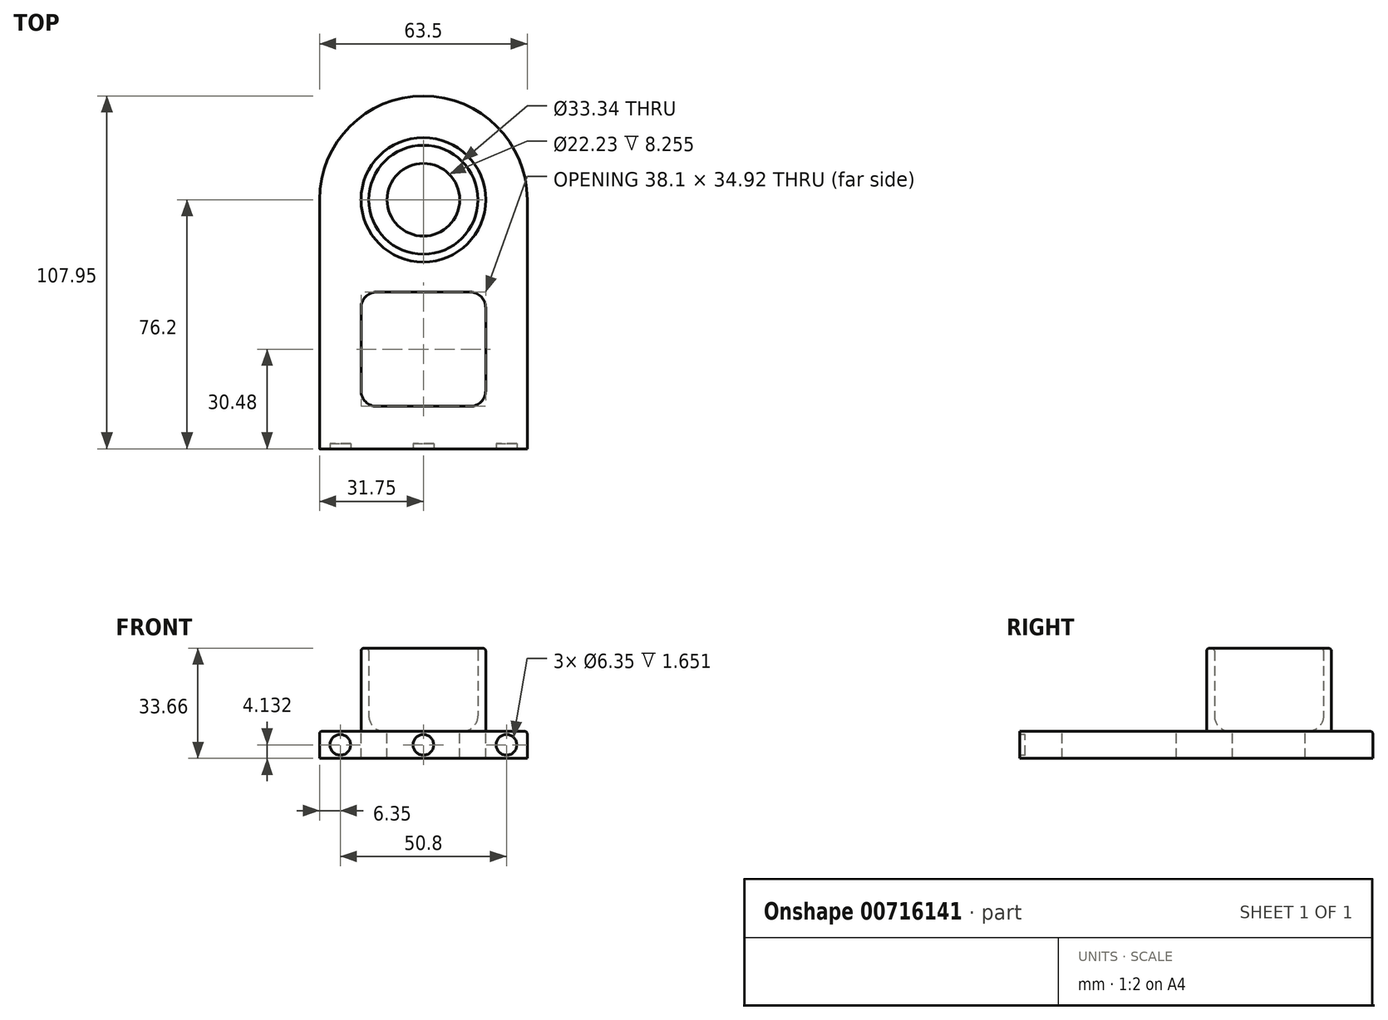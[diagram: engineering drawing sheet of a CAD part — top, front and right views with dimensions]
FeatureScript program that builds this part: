
annotation { "Feature Type Name" : "Feature", "Feature Type Description" : "" }
export const myFeature = defineFeature(function(context is Context, id is Id, definition is map)
    precondition{}
    {
        {
            var Q0;
            Q0=qCreatedBy(makeId("Top.planeOp"),FACE);
            var sketch = newSketch(context, id + "F0", { "sketchPlane" : qUnion([Q0])});
            skCircle(sketch, "E0", {"center": v(0, 0) * mm, "radius": 19.05 * mm, "construction": true});
            skArc(sketch, "E1", {"start": v(0, 31.75) * mm, "mid": v(-22.45, 22.45) * mm, "end": v(-31.75, 0) * mm});
            skLineSegment(sketch, "E2", {"start": v(-31.75, 0) * mm, "end": v(-31.75, -76.2) * mm});
            skLineSegment(sketch, "E3", {"start": v(-31.75, -76.2) * mm, "end": v(0, -76.2) * mm});
            skLineSegment(sketch, "E4", {"start": v(0, -76.2) * mm, "end": v(0, 0) * mm, "construction": true});
            skArc(sketch, "E5.MirrorCS", {"start": v(0, 31.75) * mm, "mid": v(22.45, 22.45) * mm, "end": v(31.75, 0) * mm});
            skLineSegment(sketch, "E6.MirrorCS", {"start": v(31.75, 0) * mm, "end": v(31.75, -76.2) * mm});
            skLineSegment(sketch, "E7.MirrorCS", {"start": v(31.75, -76.2) * mm, "end": v(0, -76.2) * mm});
            skSolve(sketch);
        }
        {
            var Q0;
            Q0 = qSketchRegion(id + "F0", true);
            extrude(context, id + "F1", {"entities" : qUnion([Q0]), "oppositeDirection" : true, "depth" : 8.25 * mm, "offsetDistance" : 25.4 * mm});
        }
        {
            var Q0;
            Q0=makeQuery(id+"F1.opExtrude","CAP_FACE",FACE,{"disambiguationData":[OSD([sQuery(id+"F0.wireOp",EDGE,"E1"),sQuery(id+"F0.wireOp",EDGE,"E2"),sQuery(id+"F0.wireOp",EDGE,"E3"),sQuery(id+"F0.wireOp",EDGE,"E5.MirrorCS"),sQuery(id+"F0.wireOp",EDGE,"E6.MirrorCS"),sQuery(id+"F0.wireOp",EDGE,"E7.MirrorCS")])],"isStart":true});
            var sketch = newSketch(context, id + "F2", { "sketchPlane" : qUnion([Q0])});
            skCircle(sketch, "E8", {"center": v(0, 0) * mm, "radius": 19.05 * mm});
            skCircle(sketch, "E9", {"center": v(0, 0) * mm, "radius": 16.67 * mm});
            skSolve(sketch);
        }
        {
            var Q0;
            Q0 = qSketchRegion(id + "F2", true);
            extrude(context, id + "F3", {"entities" : qUnion([Q0]), "operationType" : NewBodyOperationType.ADD, "depth" : 25.4 * mm, "offsetDistance" : 25.4 * mm});
        }
        {
            var Q0;
            Q0=makeQuery(id+"F1.opExtrude","SWEPT_FACE",FACE,{"disambiguationData":[OSD([sQuery(id+"F0.wireOp",EDGE,"E3"),sQuery(id+"F0.wireOp",EDGE,"E7.MirrorCS")])]});
            var sketch = newSketch(context, id + "F4", { "sketchPlane" : qUnion([Q0])});
            skCircle(sketch, "E10", {"center": v(-25.4, -4.13) * mm, "radius": 3.18 * mm});
            skCircle(sketch, "E11", {"center": v(0, -4.13) * mm, "radius": 3.18 * mm});
            skLineSegment(sketch, "E12", {"start": v(0, 0) * mm, "end": v(0, -8.26) * mm, "construction": true});
            skCircle(sketch, "E13.MirrorC", {"center": v(25.4, -4.13) * mm, "radius": 3.18 * mm});
            skSolve(sketch);
        }
        {
            var Q0;
            Q0 = qSketchRegion(id + "F4", true);
            extrude(context, id + "F5", {"entities" : qUnion([Q0]), "operationType" : NewBodyOperationType.REMOVE, "oppositeDirection" : true, "depth" : 1.65 * mm, "offsetDistance" : 25.4 * mm});
        }
        {
            var Q0;
            Q0=makeQuery(id+"F0.imprint","IMPRINT",FACE,{"disambiguationData":[TD([[makeQuery(id+"F0.imprint","IMPRINT",EDGE,{"derivedFrom":sQuery(id+"F0.wireOp",EDGE,"E1")}),1.0]])]});
            var sketch = newSketch(context, id + "F6", { "sketchPlane" : qUnion([Q0])});
            skLineSegment(sketch, "E14.bottom", {"start": v(-19.05, -63.18) * mm, "end": v(19.05, -63.18) * mm});
            skLineSegment(sketch, "E14.top", {"start": v(-19.05, -28.26) * mm, "end": v(19.05, -28.26) * mm});
            skLineSegment(sketch, "E14.left", {"start": v(-19.05, -63.18) * mm, "end": v(-19.05, -28.26) * mm});
            skLineSegment(sketch, "E14.right", {"start": v(19.05, -63.18) * mm, "end": v(19.05, -28.26) * mm});
            skPoint(sketch, "E14.middle", {"position": v(0, -45.72) * mm});
            skCircle(sketch, "E15", {"center": v(0, 0) * mm, "radius": 11.11 * mm});
            skSolve(sketch);
        }
        {
            var Q0;
            Q0 = qSketchRegion(id + "F6", true);
            extrude(context, id + "F7", {"entities" : qUnion([Q0]), "operationType" : NewBodyOperationType.REMOVE, "endBound" : BoundingType.UP_TO_NEXT, "oppositeDirection" : true, "depth" : 25.4 * mm, "offsetDistance" : 25.4 * mm});
        }
        {
            var Q0;
            Q0=makeQuery(id+"F3.opExtrude","CAP_EDGE",EDGE,{"disambiguationData":[OSD([sQuery(id+"F2.wireOp",EDGE,"E8")])],"isStart":true});
            var Q1;
            Q1=makeQuery(id+"F3.opExtrude","CAP_EDGE",EDGE,{"disambiguationData":[OSD([sQuery(id+"F2.wireOp",EDGE,"E9")])],"isStart":true});
            var Q2;
            Q2=makeQuery(id+"F7.boolean.opBoolean","COPY",EDGE,{"derivedFrom":makeQuery(id+"F7.opExtrude","SWEPT_EDGE",EDGE,{"disambiguationData":[OSD([sQuery(id+"F6.wireOp",EDGE,"E14.top"),sQuery(id+"F6.wireOp",EDGE,"E14.left")])]})});
            var Q3;
            Q3=makeQuery(id+"F7.boolean.opBoolean","COPY",EDGE,{"derivedFrom":makeQuery(id+"F7.opExtrude","SWEPT_EDGE",EDGE,{"disambiguationData":[OSD([sQuery(id+"F6.wireOp",EDGE,"E14.top"),sQuery(id+"F6.wireOp",EDGE,"E14.right")])]})});
            var Q4;
            Q4=makeQuery(id+"F7.boolean.opBoolean","COPY",EDGE,{"derivedFrom":makeQuery(id+"F7.opExtrude","SWEPT_EDGE",EDGE,{"disambiguationData":[OSD([sQuery(id+"F6.wireOp",EDGE,"E14.bottom"),sQuery(id+"F6.wireOp",EDGE,"E14.left")])]})});
            var Q5;
            Q5=makeQuery(id+"F7.boolean.opBoolean","COPY",EDGE,{"derivedFrom":makeQuery(id+"F7.opExtrude","SWEPT_EDGE",EDGE,{"disambiguationData":[OSD([sQuery(id+"F6.wireOp",EDGE,"E14.bottom"),sQuery(id+"F6.wireOp",EDGE,"E14.right")])]})});
            fillet(context, id + "F8", {"entities" : qUnion([Q0, Q1, Q2, Q3, Q4, Q5]), "radius" : 4.76 * mm, "tangentPropagation" : true, "allowEdgeOverflow" : false});
        }
        {
            var Q0;
            Q0=makeQuery(id+"F3.opExtrude","CAP_FACE",FACE,{"disambiguationData":[OSD([sQuery(id+"F2.wireOp",EDGE,"E8"),sQuery(id+"F2.wireOp",EDGE,"E9")])],"isStart":false});
            var Q1;
            Q1=makeQuery(id+"F1.opExtrude","CAP_EDGE",EDGE,{"disambiguationData":[OSD([sQuery(id+"F0.wireOp",EDGE,"E2")])],"isStart":true});
            fillet(context, id + "F9", {"entities" : qUnion([Q0, Q1]), "radius" : 0.8 * mm, "tangentPropagation" : true, "allowEdgeOverflow" : false});
        }
    });
